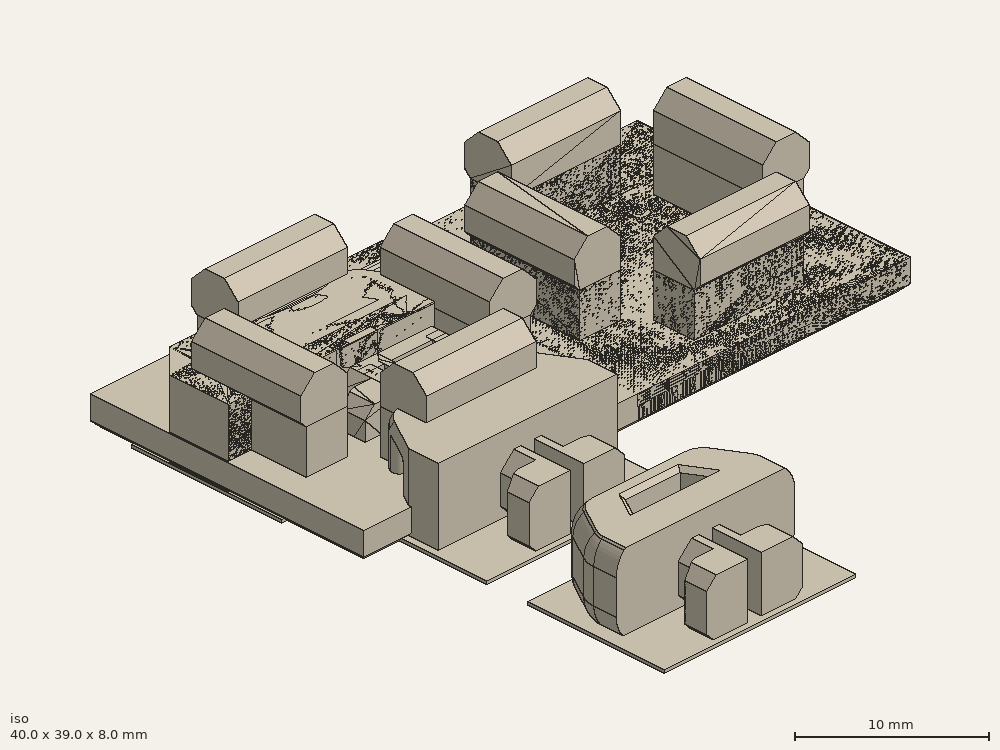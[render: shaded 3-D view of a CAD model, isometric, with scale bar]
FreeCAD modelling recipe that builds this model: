
FCSTD DOCUMENT  (FreeCAD 0.18R16146 (Git))
Label: cap-and-cable-mounter
License: All rights reserved
LicenseURL: http://en.wikipedia.org/wiki/All_rights_reserved
objects: Part::Box×28, Part::Chamfer×16, Part::Feature×16, Part::MultiFuse×14, Part::Cut×4
note: 78 computed .brp shape members not serialized (recipe doc carries the construction recipe); baked Part::Feature solids carry a one-line shape summary decoded from their .brp

FEATURE [Part::Box] Box  label="Cube"
  AttacherType = Attacher::AttachEngine3D
  Height = 2
  Length = 40
  Placement = pos=(-10,-10,0) rot=(0,0,1;0rad)
  Width = 20
FEATURE [Part::Box] Box001  label="Cube001"
  AttacherType = Attacher::AttachEngine3D
  Height = 5
  Length = 8
  Placement = pos=(-4,5.2,0) rot=(0,0,1;0rad)
  Width = 3
FEATURE [Part::Box] Box002  label="Cube002"
  AttacherType = Attacher::AttachEngine3D
  Height = 5
  Length = 8
  Placement = pos=(-4,-8.2,0) rot=(0,0,1;0rad)
  Width = 3
FEATURE [Part::Box] Box003  label="Cube003"
  AttacherType = Attacher::AttachEngine3D
  Height = 4
  Length = 1.5
  Width = 2
FEATURE [Part::Box] Box004  label="Cube004"
  AttacherType = Attacher::AttachEngine3D
  Height = 4
  Length = 1.5
  Placement = pos=(2.5,0,0) rot=(0,0,1;0rad)
  Width = 2
FEATURE [Part::Box] Box005  label="Cube005"
  AttacherType = Attacher::AttachEngine3D
  Height = 4
  Length = 6
  Placement = pos=(-1,-1,0) rot=(0,0,1;0rad)
  Width = 1
FEATURE [Part::Box] Box006  label="Cube006"
  AttacherType = Attacher::AttachEngine3D
  Height = 4
  Length = 6
  Placement = pos=(-1,-3.5,0) rot=(0,0,1;0rad)
  Width = 1
FEATURE [Part::Box] Box007  label="Cube007"
  AttacherType = Attacher::AttachEngine3D
  Height = 4
  Length = 1
  Placement = pos=(-1,-3.5,0) rot=(0,0,1;0rad)
  Width = 3
FEATURE [Part::Box] Box008  label="Cube008"
  AttacherType = Attacher::AttachEngine3D
  Height = 4
  Length = 1
  Placement = pos=(4,-3.5,0) rot=(0,0,1;0rad)
  Width = 3
FEATURE [Part::Box] Box009  label="Cube009"
  AttacherType = Attacher::AttachEngine3D
  Height = 4
  Length = 3
  Placement = pos=(2.5,1.5,0) rot=(0,0,1;0rad)
  Width = 2
FEATURE [Part::Box] Box010  label="Cube010"
  AttacherType = Attacher::AttachEngine3D
  Height = 4
  Length = 3
  Placement = pos=(-1.5,1.5,0) rot=(0,0,1;0rad)
  Width = 2
FEATURE [Part::Chamfer] Chamfer
  Base = -> Box010
  Edges = 1 edges: [Edge1 r1=0.4 r2=1.2]
FEATURE [Part::Chamfer] Chamfer001
  Base = -> Box009
  Edges = 1 edges: [Edge5 r1=0.4 r2=1.2]
FEATURE [Part::Chamfer] Chamfer002
  Base = -> Chamfer
  Edges = 2 edges r=0.7: [Edge1,Edge4]
  Placement = pos=(0,0.1,0) rot=(0,0,1;0rad)
FEATURE [Part::Chamfer] Chamfer003
  Base = -> Chamfer001
  Edges = 2 edges r=0.7: [Edge1,Edge4]
  Placement = pos=(0,0.1,0) rot=(0,0,1;0rad)
FEATURE [Part::Box] Box011  label="Cube011"
  AttacherType = Attacher::AttachEngine3D
  Height = 3
  Length = 8
  Placement = pos=(-4,5.2,5) rot=(0,0,1;0rad)
  Width = 3.4
FEATURE [Part::Box] Box012  label="Cube012"
  AttacherType = Attacher::AttachEngine3D
  Height = 3
  Length = 8
  Placement = pos=(-4,-8.6,5) rot=(0,0,1;0rad)
  Width = 3.4
FEATURE [Part::Chamfer] Chamfer009002
  Base = -> Box012
  Edges = 1 edges r=0.4: [Edge9]
FEATURE [Part::Chamfer] Chamfer009003
  Base = -> Box011
  Edges = 1 edges r=0.4: [Edge11]
FEATURE [Part::Chamfer] Chamfer009005
  Base = -> Box003
  Edges = 2 edges r=1: [Edge2,Edge4]
FEATURE [Part::Chamfer] Chamfer009006
  Base = -> Box004
  Edges = 2 edges r=1: [Edge6,Edge8]
FEATURE [Part::Box] Box013  label="Cube013"
  AttacherType = Attacher::AttachEngine3D
  Height = 5
  Length = 3
  Placement = pos=(-8.2,-4,0) rot=(0,0,1;0rad)
  Width = 8
FEATURE [Part::Box] Box014  label="Cube014"
  AttacherType = Attacher::AttachEngine3D
  Height = 5
  Length = 3
  Placement = pos=(5.2,-4,0) rot=(0,0,1;0rad)
  Width = 8
FEATURE [Part::Box] Box015  label="Cube015"
  AttacherType = Attacher::AttachEngine3D
  Height = 3
  Length = 3.4
  Placement = pos=(-8.6,-4,5) rot=(0,0,1;0rad)
  Width = 8
FEATURE [Part::Box] Box016  label="Cube016"
  AttacherType = Attacher::AttachEngine3D
  Height = 3
  Length = 3.4
  Placement = pos=(5.2,-4,5) rot=(0,0,1;0rad)
  Width = 8
FEATURE [Part::Chamfer] Chamfer009007
  Base = -> Box015
  Edges = 1 edges r=0.4: [Edge4]
FEATURE [Part::Chamfer] Chamfer009008
  Base = -> Box016
  Edges = 1 edges r=0.4: [Edge8]
FEATURE [Part::Chamfer] Chamfer009009
  Base = -> Chamfer009007
  Edges = 2 edges r=1: [Edge3,Edge12]
FEATURE [Part::Chamfer] Chamfer009010
  Base = -> Chamfer009003
  Edges = 2 edges r=1: [Edge8,Edge12]
FEATURE [Part::Chamfer] Chamfer009011
  Base = -> Chamfer009008
  Edges = 2 edges r=1: [Edge3,Edge11]
FEATURE [Part::Chamfer] Chamfer009012
  Base = -> Chamfer009002
  Edges = 2 edges r=1: [Edge8,Edge11]
FEATURE [Part::MultiFuse] Fusion  label="arm-2"
  Shapes = -> [Chamfer009009,Box013]
FEATURE [Part::MultiFuse] Fusion004  label="arm-6"
  Shapes = -> [Chamfer009010,Box001]
FEATURE [Part::MultiFuse] Fusion005
  Shapes = -> [Chamfer009011,Box014]
FEATURE [Part::MultiFuse] Fusion006  label="arm-1"
  Shapes = -> [Chamfer009012,Box002]
FEATURE [Part::MultiFuse] Fusion008
  Shapes = -> [Chamfer009006,Box007,Chamfer003,Box008,Box006,Box005,Chamfer009005,Chamfer002]
FEATURE [Part::Feature] Fusion009
  Placement = pos=(20,0,0) rot=(0,0,1;0rad)
  shape: bbox 3.4 x 8 x 8 mm, 13 faces (baked)
FEATURE [Part::Feature] Fusion006001  label="arm-5"
  Placement = pos=(20,0,0) rot=(0,0,1;0rad)
  shape: bbox 8 x 3.4 x 8 mm, 13 faces (baked)
FEATURE [Part::Feature] Fusion004001  label="arm-4"
  Placement = pos=(20,0,0) rot=(0,0,1;0rad)
  shape: bbox 8 x 3.4 x 8 mm, 13 faces (baked)
FEATURE [Part::Feature] Fusion005001  label="arm-3"
  Placement = pos=(20,0,0) rot=(0,0,1;0rad)
  shape: bbox 3.4 x 8 x 8 mm, 13 faces (baked)
FEATURE [Part::Chamfer] Chamfer009013  label="plate"
  Base = -> Box
  Edges = 4 edges r=0.4: [Edge4,Edge8,Edge9,Edge11]
FEATURE [Part::Feature] Part__Feature  label="cable_clip_horizontal v1"
  Placement = pos=(0,-20,-30) rot=(0,0,1;0rad)
  shape: bbox 13.05 x 10.94 x 5.4 mm, 92 faces (baked)
FEATURE [Part::Feature] Part__Feature001  label="cable_clip_lcd v1"
  Placement = pos=(0,-20,-70) rot=(0,0,1;0rad)
  shape: bbox 19.81 x 12.04 x 6.352 mm, 81 faces (baked)
FEATURE [Part::Feature] Part__Feature002  label="cable_clip_vertical v1"
  Placement = pos=(0,-20,-50) rot=(0,0,1;0rad)
  shape: bbox 13.05 x 11.6 x 6.819 mm, 67 faces (baked)
FEATURE [Part::Feature] Fusion008001  label="Fusion006003"
  Placement = pos=(2,0,0) rot=(0,0,1;3.14159rad)
  shape: bbox 7.003 x 7.103 x 4.003 mm, 32 faces (baked)
FEATURE [Part::Box] Box017  label="Cube017"
  AttacherType = Attacher::AttachEngine3D
  Height = 10
  Length = 20
  Placement = pos=(-10,0,0) rot=(0,0,1;0rad)
  Width = 10
FEATURE [Part::Box] Box018  label="Cube018"
  AttacherType = Attacher::AttachEngine3D
  Height = 10
  Length = 20
  Placement = pos=(-10,-10,0) rot=(0,0,1;0rad)
  Width = 10
FEATURE [Part::Cut] Cut
  Base = -> Fusion008001
  Tool = -> Box017
FEATURE [Part::Box] Box020  label="Cube020"
  AttacherType = Attacher::AttachEngine3D
  Height = 10
  Length = 20
  Placement = pos=(-10,-10,0) rot=(0,0,1;0rad)
  Width = 10
FEATURE [Part::Box] Box021  label="Cube021"
  AttacherType = Attacher::AttachEngine3D
  Height = 10
  Length = 20
  Placement = pos=(-10,-10,0) rot=(0,0,1;0rad)
  Width = 10
FEATURE [Part::Cut] Cut001
  Base = -> Part__Feature002
  Tool = -> Box018
FEATURE [Part::Cut] Cut002
  Base = -> Part__Feature001
  Tool = -> Box020
FEATURE [Part::Cut] Cut003
  Base = -> Part__Feature
  Tool = -> Box021
FEATURE [Part::Box] Box022  label="Cube022"
  AttacherType = Attacher::AttachEngine3D
  Height = 5.4
  Length = 4
  Placement = pos=(-2,0,0) rot=(0,0,1;0rad)
  Width = 1
FEATURE [Part::Box] Box023  label="Cube023"
  AttacherType = Attacher::AttachEngine3D
  Height = 5.4
  Length = 4
  Placement = pos=(-2,0,0) rot=(0,0,1;0rad)
  Width = 1
FEATURE [Part::Box] Box024  label="Cube024"
  AttacherType = Attacher::AttachEngine3D
  Height = 5.4
  Length = 4
  Placement = pos=(-2,0,0) rot=(0,0,1;0rad)
  Width = 1
FEATURE [Part::MultiFuse] Fusion008002
  Shapes = -> [Cut003,Box022]
FEATURE [Part::MultiFuse] Fusion008003
  Shapes = -> [Box023,Cut002]
FEATURE [Part::MultiFuse] Fusion008004
  Shapes = -> [Cut001,Box024]
FEATURE [Part::Feature] Cut004
  shape: bbox 7.003 x 3.603 x 4.003 mm, 26 faces, 2 solids (baked)
FEATURE [Part::Feature] Cut005
  shape: bbox 7 x 3.6 x 4 mm, 26 faces, 2 solids (baked)
FEATURE [Part::MultiFuse] Fusion008005  label="cable-clip-horizontal"
  Shapes = -> [Cut,Fusion008002]
FEATURE [Part::MultiFuse] Fusion008006  label="cable-clip-vertical"
  Shapes = -> [Cut004,Fusion008004]
FEATURE [Part::MultiFuse] Fusion008007  label="cable-clip-lcd"
  Shapes = -> [Cut005,Fusion008003]
FEATURE [Part::Feature] Fusion008005001  label="cable-clip-horizontal001"
  Placement = pos=(0,-25,0) rot=(0,0,1;0rad)
  shape: bbox 13.05 x 9.143 x 5.403 mm, 80 faces (baked)
FEATURE [Part::Feature] Fusion008006001  label="cable-clip-vertical001"
  Placement = pos=(0,-12,0) rot=(0,0,1;0rad)
  shape: bbox 13.05 x 9.796 x 6.819 mm, 55 faces (baked)
FEATURE [Part::Feature] Fusion008007001  label="cable-clip-lcd001"
  shape: bbox 19.81 x 10.24 x 6.352 mm, 68 faces (baked)
FEATURE [Part::Box] Box025  label="Cube025"
  AttacherType = Attacher::AttachEngine3D
  Height = 0.2
  Length = 20
  Placement = pos=(-10,-4,0) rot=(0,0,1;0rad)
  Width = 11
FEATURE [Part::Box] Box026  label="Cube026"
  AttacherType = Attacher::AttachEngine3D
  Height = 0.2
  Length = 14
  Placement = pos=(-7,-16,0) rot=(0,0,1;0rad)
  Width = 11
FEATURE [Part::Box] Box027  label="Cube027"
  AttacherType = Attacher::AttachEngine3D
  Height = 0.2
  Length = 14
  Placement = pos=(-7,-29,0) rot=(0,0,1;0rad)
  Width = 10
FEATURE [Part::MultiFuse] Fusion008007002
  Shapes = -> [Box027,Fusion008005001]
FEATURE [Part::MultiFuse] Fusion008007003
  Shapes = -> [Box026,Fusion008006001]
FEATURE [Part::Box] Box028  label="Cube028"
  AttacherType = Attacher::AttachEngine3D
  Height = 2
  Length = 20
  Placement = pos=(10,-10,0) rot=(0,0,1;0rad)
  Width = 20
FEATURE [Part::Feature] Fusion006001001  label="Fusion008007004"
  Placement = pos=(20,0,0) rot=(0,0,1;0rad)
  shape: bbox 8 x 3.4 x 8 mm, 13 faces (baked)
FEATURE [Part::Feature] Fusion009001  label="Fusion008007005"
  Placement = pos=(20,0,0) rot=(0,0,1;0rad)
  shape: bbox 3.4 x 8 x 8 mm, 13 faces (baked)
FEATURE [Part::Feature] Fusion004001001  label="Fusion008007006"
  Placement = pos=(20,0,0) rot=(0,0,1;0rad)
  shape: bbox 8 x 3.4 x 8 mm, 13 faces (baked)
FEATURE [Part::Chamfer] Chamfer009014
  Base = -> Box028
  Edges = 4 edges r=0.4: [Edge4,Edge8,Edge9,Edge11]
FEATURE [Part::MultiFuse] Fusion008007004  label="Fusion008007007"
  Shapes = -> [Chamfer009014,Fusion009001,Fusion004001001,Fusion006001001]
